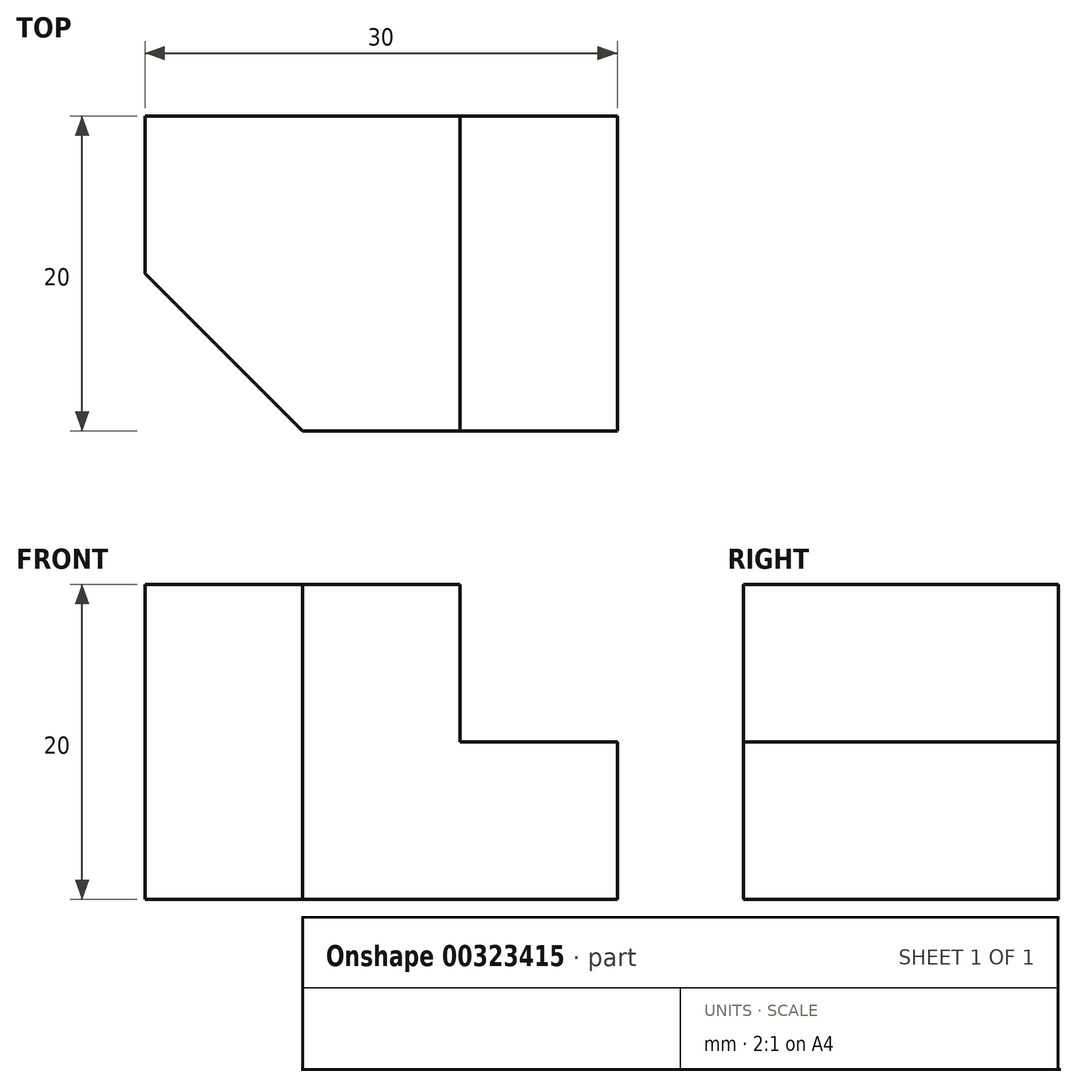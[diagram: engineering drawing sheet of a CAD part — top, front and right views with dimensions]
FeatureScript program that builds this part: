
annotation { "Feature Type Name" : "Feature", "Feature Type Description" : "" }
export const myFeature = defineFeature(function(context is Context, id is Id, definition is map)
    precondition{}
    {
        {
            var Q0;
            Q0=qCreatedBy(makeId("Front.planeOp"),FACE);
            var sketch = newSketch(context, id + "F0", { "sketchPlane" : qUnion([Q0])});
            skLineSegment(sketch, "E0", {"start": v(0, 0) * mm, "end": v(0, 20) * mm});
            skLineSegment(sketch, "E1", {"start": v(0, 20) * mm, "end": v(10, 20) * mm});
            skLineSegment(sketch, "E2", {"start": v(10, 20) * mm, "end": v(10, 0) * mm});
            skLineSegment(sketch, "E3", {"start": v(10, 0) * mm, "end": v(0, 0) * mm});
            skLineSegment(sketch, "E4", {"start": v(10, 20) * mm, "end": v(20, 20) * mm});
            skLineSegment(sketch, "E5", {"start": v(20, 20) * mm, "end": v(20, 10) * mm});
            skLineSegment(sketch, "E6", {"start": v(20, 10) * mm, "end": v(30, 10) * mm});
            skLineSegment(sketch, "E7", {"start": v(30, 10) * mm, "end": v(30, 0) * mm});
            skLineSegment(sketch, "E8", {"start": v(30, 0) * mm, "end": v(10, 0) * mm});
            skSolve(sketch);
        }
        {
            var Q0;
            Q0=makeQuery(id+"F0.imprint","IMPRINT",FACE,{"disambiguationData":[TD([[makeQuery(id+"F0.imprint","IMPRINT",EDGE,{"derivedFrom":sQuery(id+"F0.wireOp",EDGE,"E2")}),1.0]])]});
            var Q1;
            Q1=makeQuery(id+"F0.imprint","IMPRINT",FACE,{"disambiguationData":[TD([[makeQuery(id+"F0.imprint","IMPRINT",EDGE,{"derivedFrom":sQuery(id+"F0.wireOp",EDGE,"E0")}),-1.0]])]});
            extrude(context, id + "F1", {"entities" : qUnion([Q0, Q1]), "depth" : 20 * mm, "symmetric" : true});
        }
        {
            var Q0;
            Q0=makeQuery(id+"F1.opExtrude","SWEPT_FACE",FACE,{"disambiguationData":[OSD([sQuery(id+"F0.wireOp",EDGE,"E1"),sQuery(id+"F0.wireOp",EDGE,"E4")])]});
            var sketch = newSketch(context, id + "F2", { "sketchPlane" : qUnion([Q0])});
            skLineSegment(sketch, "E9", {"start": v(0, 0) * mm, "end": v(10, -10) * mm});
            skLineSegment(sketch, "E10", {"start": v(10, -10) * mm, "end": v(0, -10) * mm});
            skLineSegment(sketch, "E11", {"start": v(0, -10) * mm, "end": v(0, 0) * mm});
            skSolve(sketch);
        }
        {
            var Q0;
            Q0=makeQuery(id+"F2.imprint","IMPRINT",FACE,{"disambiguationData":[TD([[makeQuery(id+"F2.imprint","IMPRINT",EDGE,{"derivedFrom":sQuery(id+"F2.wireOp",EDGE,"E9")}),-1.0]])]});
            extrude(context, id + "F3", {"entities" : qUnion([Q0]), "operationType" : NewBodyOperationType.REMOVE, "endBound" : BoundingType.THROUGH_ALL, "oppositeDirection" : true, "depth" : 25 * mm});
        }
    });
